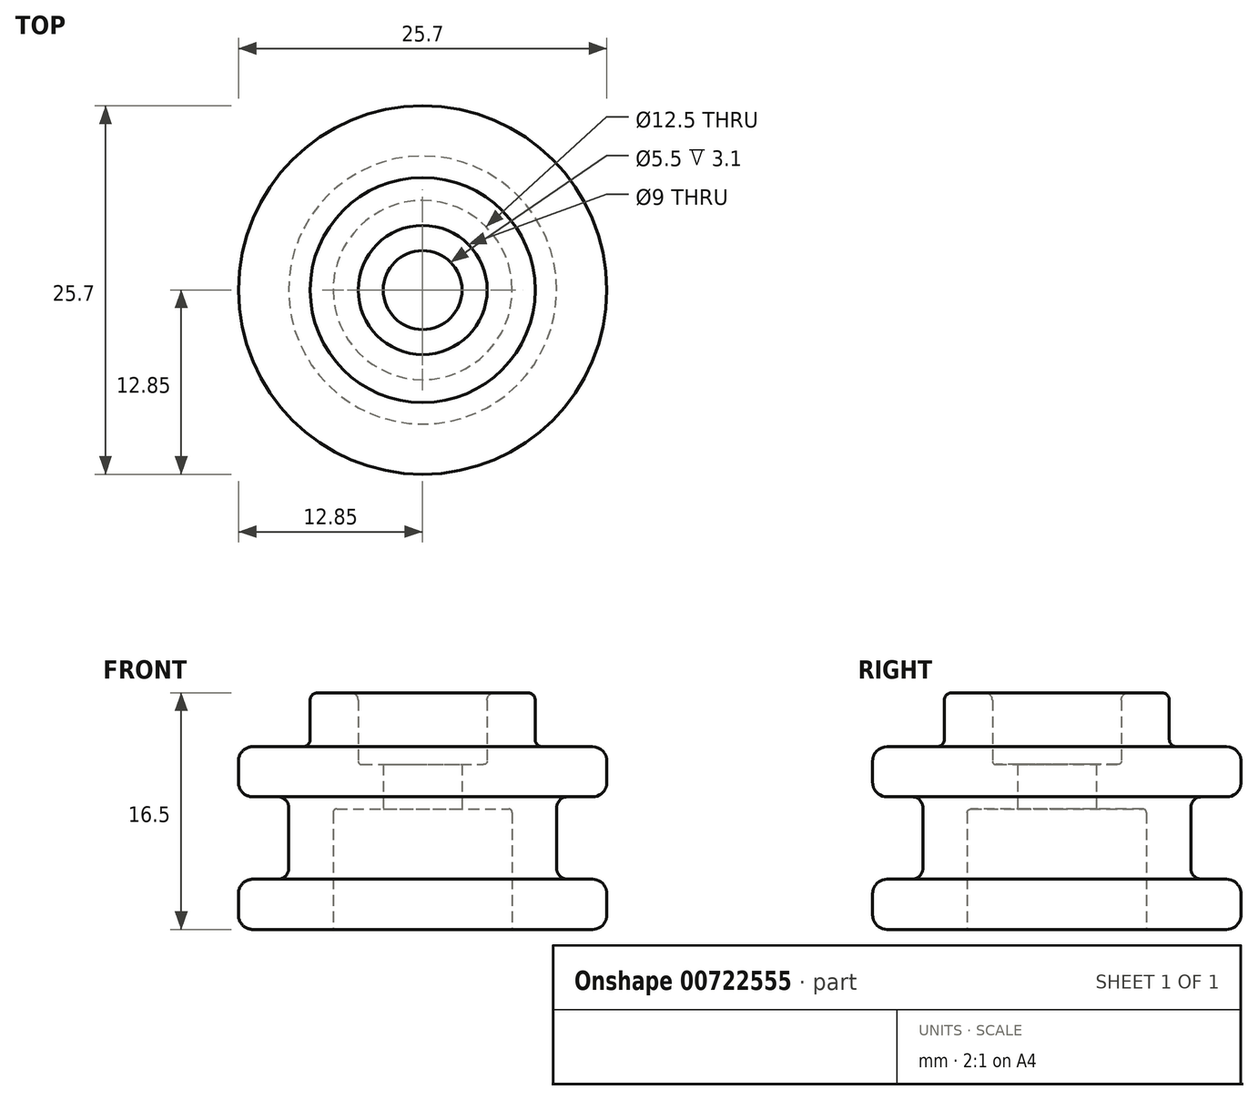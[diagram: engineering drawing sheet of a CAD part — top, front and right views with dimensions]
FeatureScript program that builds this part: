
annotation { "Feature Type Name" : "Feature", "Feature Type Description" : "" }
export const myFeature = defineFeature(function(context is Context, id is Id, definition is map)
    precondition{}
    {
        {
            var Q0;
            Q0=qCreatedBy(makeId("Front.planeOp"),FACE);
            var sketch = newSketch(context, id + "F0", { "sketchPlane" : qUnion([Q0])});
            skLineSegment(sketch, "E0", {"start": v(0, 0) * mm, "end": v(-6.25, 0) * mm});
            skLineSegment(sketch, "E1", {"start": v(-6.25, 0) * mm, "end": v(-11.85, 0) * mm});
            skLineSegment(sketch, "E2", {"start": v(-12.85, 1) * mm, "end": v(-12.85, 2.5) * mm});
            skLineSegment(sketch, "E3", {"start": v(-11.85, 3.5) * mm, "end": v(-10.1, 3.5) * mm});
            skLineSegment(sketch, "E4", {"start": v(-9.35, 4.25) * mm, "end": v(-9.35, 8.5) * mm});
            skLineSegment(sketch, "E5", {"start": v(-10.1, 9.25) * mm, "end": v(-11.85, 9.25) * mm});
            skLineSegment(sketch, "E6", {"start": v(-12.85, 10.25) * mm, "end": v(-12.85, 11.75) * mm});
            skLineSegment(sketch, "E7", {"start": v(-11.85, 12.75) * mm, "end": v(-8.35, 12.75) * mm});
            skLineSegment(sketch, "E8", {"start": v(-7.85, 13.25) * mm, "end": v(-7.85, 16) * mm});
            skLineSegment(sketch, "E9", {"start": v(-7.35, 16.5) * mm, "end": v(-5, 16.5) * mm});
            skLineSegment(sketch, "E10", {"start": v(-4.5, 16) * mm, "end": v(-4.5, 11.75) * mm});
            skLineSegment(sketch, "E11", {"start": v(-6.25, 0) * mm, "end": v(-6.25, 8.15) * mm});
            skLineSegment(sketch, "E12", {"start": v(-6, 8.4) * mm, "end": v(-2.75, 8.4) * mm});
            skLineSegment(sketch, "E13", {"start": v(-2.75, 8.4) * mm, "end": v(-2.75, 11.5) * mm});
            skLineSegment(sketch, "E14", {"start": v(-2.75, 11.5) * mm, "end": v(-4.25, 11.5) * mm});
            skPoint(sketch, "E15.visualSharp", {"position": v(-4.5, 16.5) * mm});
            skPoint(sketch, "E16.visualSharp", {"position": v(-7.85, 12.75) * mm});
            skArc(sketch, "E16.filletArc", {"start": v(-8.35, 12.75) * mm, "mid": v(-8, 12.9) * mm, "end": v(-7.85, 13.25) * mm});
            skPoint(sketch, "E17.visualSharp", {"position": v(-7.85, 16.5) * mm});
            skArc(sketch, "E17.filletArc", {"start": v(-7.35, 16.5) * mm, "mid": v(-7.7, 16.35) * mm, "end": v(-7.85, 16) * mm});
            skPoint(sketch, "E18.visualSharp", {"position": v(-12.85, 12.75) * mm});
            skArc(sketch, "E18.filletArc", {"start": v(-11.85, 12.75) * mm, "mid": v(-12.56, 12.46) * mm, "end": v(-12.85, 11.75) * mm});
            skPoint(sketch, "E19.visualSharp", {"position": v(-12.85, 9.25) * mm});
            skArc(sketch, "E19.filletArc", {"start": v(-12.85, 10.25) * mm, "mid": v(-12.56, 9.54) * mm, "end": v(-11.85, 9.25) * mm});
            skPoint(sketch, "E20.visualSharp", {"position": v(-12.85, 3.5) * mm});
            skArc(sketch, "E20.filletArc", {"start": v(-11.85, 3.5) * mm, "mid": v(-12.56, 3.2) * mm, "end": v(-12.85, 2.5) * mm});
            skPoint(sketch, "E21.visualSharp", {"position": v(-12.85, 0) * mm});
            skArc(sketch, "E21.filletArc", {"start": v(-12.85, 1) * mm, "mid": v(-12.56, 0.3) * mm, "end": v(-11.85, 0) * mm});
            skPoint(sketch, "E22.visualSharp", {"position": v(-9.35, 3.5) * mm});
            skArc(sketch, "E22.filletArc", {"start": v(-10.1, 3.5) * mm, "mid": v(-9.57, 3.72) * mm, "end": v(-9.35, 4.25) * mm});
            skPoint(sketch, "E23.visualSharp", {"position": v(-9.35, 9.25) * mm});
            skArc(sketch, "E23.filletArc", {"start": v(-9.35, 8.5) * mm, "mid": v(-9.57, 9.03) * mm, "end": v(-10.1, 9.25) * mm});
            skPoint(sketch, "E24.visualSharp", {"position": v(-6.25, 8.4) * mm});
            skArc(sketch, "E24.filletArc", {"start": v(-6, 8.4) * mm, "mid": v(-6.18, 8.33) * mm, "end": v(-6.25, 8.15) * mm});
            skPoint(sketch, "E25.visualSharp", {"position": v(-4.5, 11.5) * mm});
            skArc(sketch, "E25.filletArc", {"start": v(-4.5, 11.75) * mm, "mid": v(-4.43, 11.57) * mm, "end": v(-4.25, 11.5) * mm});
            skArc(sketch, "E26.filletArc", {"start": v(-4.5, 16) * mm, "mid": v(-4.65, 16.35) * mm, "end": v(-5, 16.5) * mm});
            skLineSegment(sketch, "E27", {"start": v(0, 0) * mm, "end": v(0, 5) * mm});
            skSolve(sketch);
        }
        {
            var Q0;
            Q0=makeQuery(id+"F0.imprint","IMPRINT",FACE,{"disambiguationData":[TD([[makeQuery(id+"F0.imprint","IMPRINT",EDGE,{"derivedFrom":sQuery(id+"F0.wireOp",EDGE,"E1")}),-1.0]])]});
            var Q1;
            Q1=sQuery(id+"F0.wireOp",EDGE,"E27");
            revolve(context, id + "F1", {"surfaceOperationType" : NewSurfaceOperationType.NEW, "entities" : qUnion([Q0]), "axis" : qUnion([Q1]), "revolveType" : RevolveType.FULL});
        }
    });
